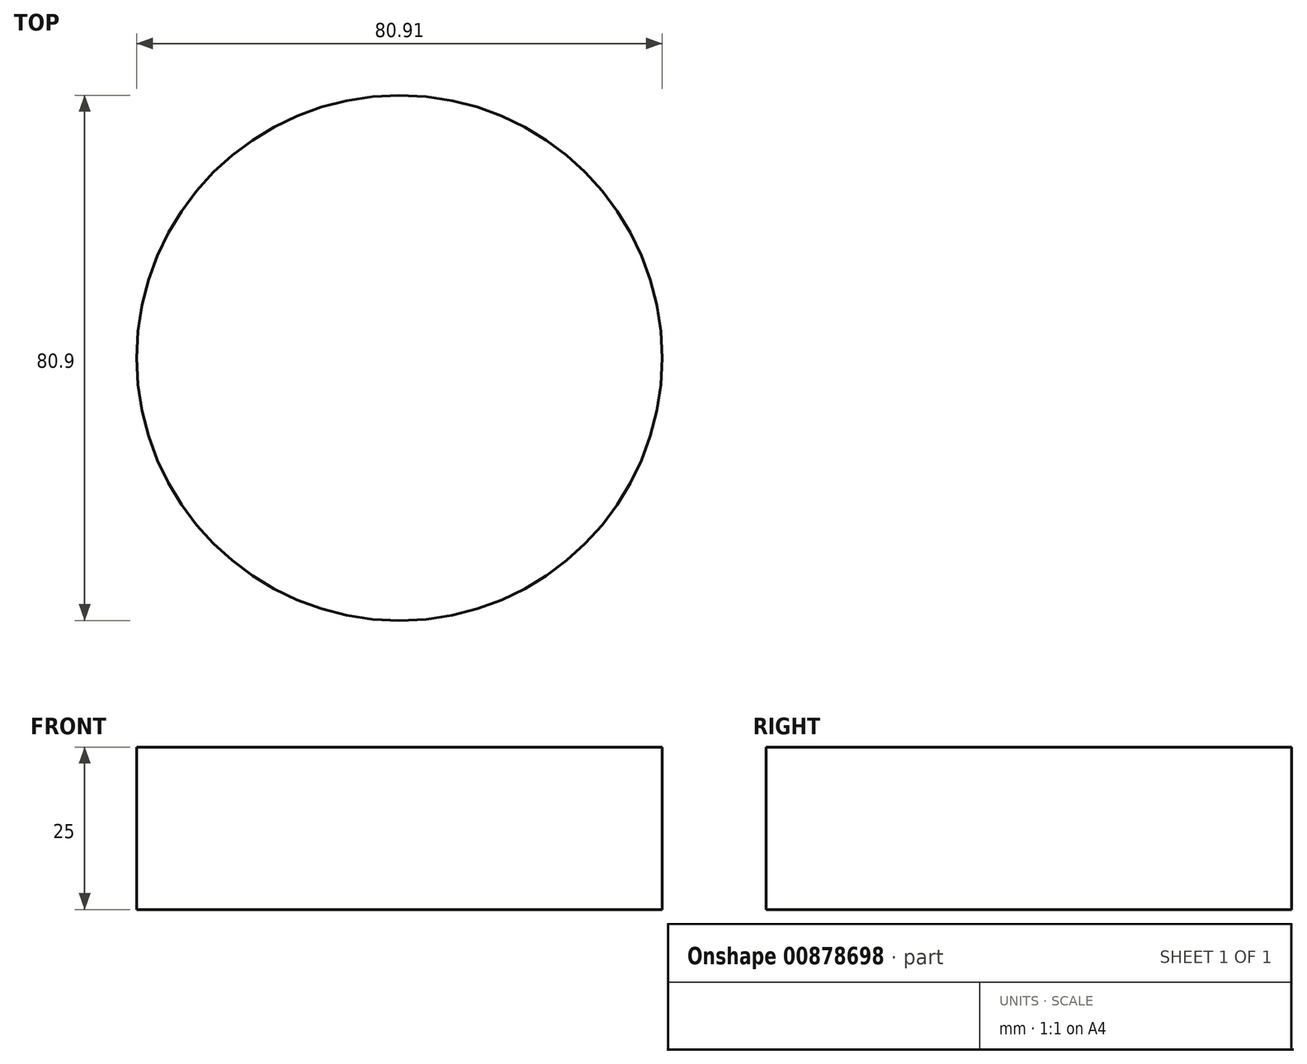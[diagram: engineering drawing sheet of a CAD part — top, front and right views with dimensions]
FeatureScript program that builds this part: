
annotation { "Feature Type Name" : "Feature", "Feature Type Description" : "" }
export const myFeature = defineFeature(function(context is Context, id is Id, definition is map)
    precondition{}
    {
        {
            var Q0;
            Q0=qCreatedBy(makeId("Top.planeOp"),FACE);
            var sketch = newSketch(context, id + "F0", { "sketchPlane" : qUnion([Q0])});
            skCircle(sketch, "E0", {"center": v(-164.55, 0) * mm, "radius": 40.45 * mm});
            skSolve(sketch);
        }
        {
            var Q0;
            Q0=makeQuery(id+"F0.imprint","IMPRINT",FACE,{"disambiguationData":[TD([[makeQuery(id+"F0.imprint","IMPRINT",EDGE,{"derivedFrom":sQuery(id+"F0.wireOp",EDGE,"E0")}),1.0]])]});
            extrude(context, id + "F1", {"entities" : qUnion([Q0]), "depth" : 25 * mm, "offsetDistance" : 25 * mm});
        }
    });
